# Revit family: PROB
name_source: partatom
category: Lighting Fixtures
units: mm (PartAtom-declared; Revit-internal decimal feet)

## family parameters
Cut with Voids When Loaded = No
Host = Face
Light Source = No
OmniClass Number = 23.80.70.14
OmniClass Title = Luminaries for External Lighting
Part Type = Normal
Room Calculation Point = No
Round Connector Dimension = Use Diameter
Shared = No

## types (13) — shared parameters
Default Elevation = 48.000"
Description = Providence Bollard - PROB
Glass = Glass-Frosted
Lamp = ED-17
Load Classification = Lighting
Manufacturer = Architectural Area Lighting
Model = PROB
URL = https://www.currentlighting.com
Watt = 25 W
Wattage Comments = 25-43W

## per-type parameters (varying)
| type | Apparent Load | Finish |
| PROB - AWT | 0 VA | Aluminum-Artic White |
| PROB - BLK | 0 VA | Aluminum-Black |
| PROB - MTB | 0 VA | Aluminum-Matte Black |
| PROB - DGN | 0 VA | Aluminum-Dark Green |
| PROB - DBZ | 0 VA | Aluminum-Dark Bronze |
| PROB - WRZ | 0 VA | Aluminum-Weathered Bronze |
| PROB - BRM | 25 VA | Aluminum-Metalic Bronze |
| PROB - VBL | 0 VA | Aluminum-Verde Blue |
| PROB - CRT | 0 VA | Corten |
| PROB - MAL | 0 VA | Aluminum-Matte |
| PROB - MDG | 0 VA | Aluminum-Medium Grey |
| PROB - ATG | 0 VA | Aluminum-Antique Green |
| PROB - LGY | 0 VA | Aluminum-Light Grey |

## geometry (parser evidence)
native form markers: Blend x33, Sweep x9
no freeform markers — native parametric forms only
